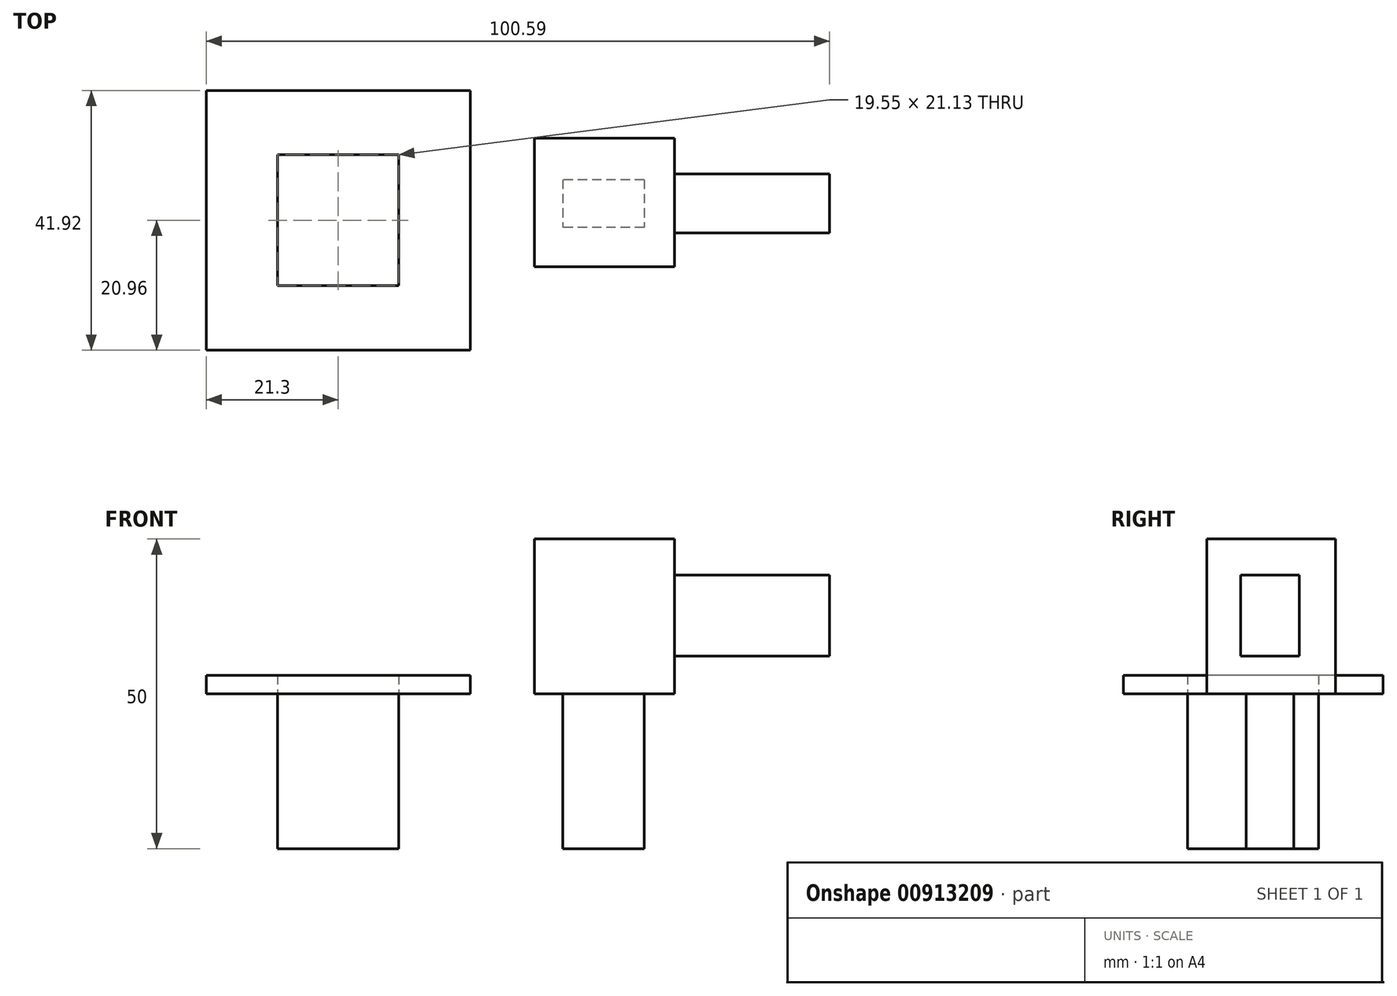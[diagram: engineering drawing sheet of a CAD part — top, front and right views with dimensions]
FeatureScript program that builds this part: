
annotation { "Feature Type Name" : "Feature", "Feature Type Description" : "" }
export const myFeature = defineFeature(function(context is Context, id is Id, definition is map)
    precondition{}
    {
        {
            var Q0;
            Q0=qCreatedBy(makeId("Top.planeOp"),FACE);
            var sketch = newSketch(context, id + "F0", { "sketchPlane" : qUnion([Q0])});
            skLineSegment(sketch, "E0.bottom", {"start": v(9.77, 10.56) * mm, "end": v(-9.77, 10.56) * mm});
            skLineSegment(sketch, "E0.top", {"start": v(9.77, -10.56) * mm, "end": v(-9.77, -10.56) * mm});
            skLineSegment(sketch, "E0.left", {"start": v(9.77, 10.56) * mm, "end": v(9.77, -10.56) * mm});
            skLineSegment(sketch, "E0.right", {"start": v(-9.77, 10.56) * mm, "end": v(-9.77, -10.56) * mm});
            skPoint(sketch, "E0.middle", {"position": v(0, 0) * mm});
            skSolve(sketch);
        }
        {
            var Q0;
            Q0 = qSketchRegion(id + "F0", true);
            extrude(context, id + "F1", {"entities" : qUnion([Q0]), "depth" : 25 * mm, "offsetDistance" : 25 * mm});
        }
        {
            var Q0;
            Q0=makeQuery(id+"F1.opExtrude","CAP_FACE",FACE,{"disambiguationData":[OSD([sQuery(id+"F0.wireOp",EDGE,"E0.bottom"),sQuery(id+"F0.wireOp",EDGE,"E0.top"),sQuery(id+"F0.wireOp",EDGE,"E0.left"),sQuery(id+"F0.wireOp",EDGE,"E0.right")])],"isStart":false});
            var sketch = newSketch(context, id + "F2", { "sketchPlane" : qUnion([Q0])});
            skLineSegment(sketch, "E1.bottom", {"start": v(21.3, 20.96) * mm, "end": v(-21.3, 20.96) * mm});
            skLineSegment(sketch, "E1.top", {"start": v(21.3, -20.96) * mm, "end": v(-21.3, -20.96) * mm});
            skLineSegment(sketch, "E1.left", {"start": v(21.3, 20.96) * mm, "end": v(21.3, -20.96) * mm});
            skLineSegment(sketch, "E1.right", {"start": v(-21.3, 20.96) * mm, "end": v(-21.3, -20.96) * mm});
            skPoint(sketch, "E1.middle", {"position": v(0, 0) * mm});
            skLineSegment(sketch, "E2.bottom", {"start": v(54.29, -7.51) * mm, "end": v(31.7, -7.51) * mm});
            skLineSegment(sketch, "E2.top", {"start": v(54.29, 13.28) * mm, "end": v(31.7, 13.28) * mm});
            skLineSegment(sketch, "E2.left", {"start": v(54.29, -7.51) * mm, "end": v(54.29, 13.28) * mm});
            skLineSegment(sketch, "E2.right", {"start": v(31.7, -7.51) * mm, "end": v(31.7, 13.28) * mm});
            skPoint(sketch, "E2.middle", {"position": v(43, 2.88) * mm});
            skSolve(sketch);
        }
        {
            var Q0;
            Q0=makeQuery(id+"F2.imprint","IMPRINT",FACE,{"disambiguationData":[TD([[makeQuery(id+"F2.imprint","IMPRINT",EDGE,{"derivedFrom":sQuery(id+"F2.wireOp",EDGE,"E1.bottom")}),1.0]])]});
            extrude(context, id + "F3", {"entities" : qUnion([Q0]), "depth" : 3 * mm, "offsetDistance" : 25 * mm});
        }
        {
            var Q0;
            Q0=makeQuery(id+"F2.imprint","IMPRINT",FACE,{"disambiguationData":[TD([[makeQuery(id+"F2.imprint","IMPRINT",EDGE,{"derivedFrom":sQuery(id+"F2.wireOp",EDGE,"E2.bottom")}),-1.0]])]});
            extrude(context, id + "F4", {"entities" : qUnion([Q0]), "depth" : 25 * mm, "offsetDistance" : 25 * mm});
        }
        {
            var Q0;
            Q0=makeQuery(id+"F4.opExtrude","CAP_FACE",FACE,{"disambiguationData":[OSD([sQuery(id+"F2.wireOp",EDGE,"E2.bottom"),sQuery(id+"F2.wireOp",EDGE,"E2.top"),sQuery(id+"F2.wireOp",EDGE,"E2.left"),sQuery(id+"F2.wireOp",EDGE,"E2.right")])],"isStart":true});
            var sketch = newSketch(context, id + "F5", { "sketchPlane" : qUnion([Q0])});
            skLineSegment(sketch, "E3.bottom", {"start": v(49.37, -6.55) * mm, "end": v(36.27, -6.55) * mm});
            skLineSegment(sketch, "E3.top", {"start": v(49.37, 1.13) * mm, "end": v(36.27, 1.13) * mm});
            skLineSegment(sketch, "E3.left", {"start": v(49.37, -6.55) * mm, "end": v(49.37, 1.13) * mm});
            skLineSegment(sketch, "E3.right", {"start": v(36.27, -6.55) * mm, "end": v(36.27, 1.13) * mm});
            skPoint(sketch, "E3.middle", {"position": v(42.82, -2.71) * mm});
            skSolve(sketch);
        }
        {
            var Q0;
            Q0=makeQuery(id+"F5.imprint","IMPRINT",FACE,{"disambiguationData":[TD([[makeQuery(id+"F5.imprint","IMPRINT",EDGE,{"derivedFrom":sQuery(id+"F5.wireOp",EDGE,"E3.bottom")}),-1.0]])]});
            extrude(context, id + "F6", {"entities" : qUnion([Q0]), "operationType" : NewBodyOperationType.ADD, "depth" : 25 * mm, "offsetDistance" : 25 * mm});
        }
        {
            var Q0;
            Q0=makeQuery(id+"F4.opExtrude","SWEPT_FACE",FACE,{"disambiguationData":[OSD([sQuery(id+"F2.wireOp",EDGE,"E2.left")])]});
            var sketch = newSketch(context, id + "F7", { "sketchPlane" : qUnion([Q0])});
            skLineSegment(sketch, "E4.bottom", {"start": v(7.46, 44.18) * mm, "end": v(-2.03, 44.18) * mm});
            skLineSegment(sketch, "E4.top", {"start": v(7.46, 31.07) * mm, "end": v(-2.03, 31.07) * mm});
            skLineSegment(sketch, "E4.left", {"start": v(7.46, 44.18) * mm, "end": v(7.46, 31.07) * mm});
            skLineSegment(sketch, "E4.right", {"start": v(-2.03, 44.18) * mm, "end": v(-2.03, 31.07) * mm});
            skPoint(sketch, "E4.middle", {"position": v(2.71, 37.62) * mm});
            skSolve(sketch);
        }
        {
            var Q0;
            Q0=makeQuery(id+"F7.imprint","IMPRINT",FACE,{"disambiguationData":[TD([[makeQuery(id+"F7.imprint","IMPRINT",EDGE,{"derivedFrom":sQuery(id+"F7.wireOp",EDGE,"E4.bottom")}),1.0]])]});
            extrude(context, id + "F8", {"entities" : qUnion([Q0]), "operationType" : NewBodyOperationType.ADD, "depth" : 25 * mm, "offsetDistance" : 25 * mm});
        }
    });
